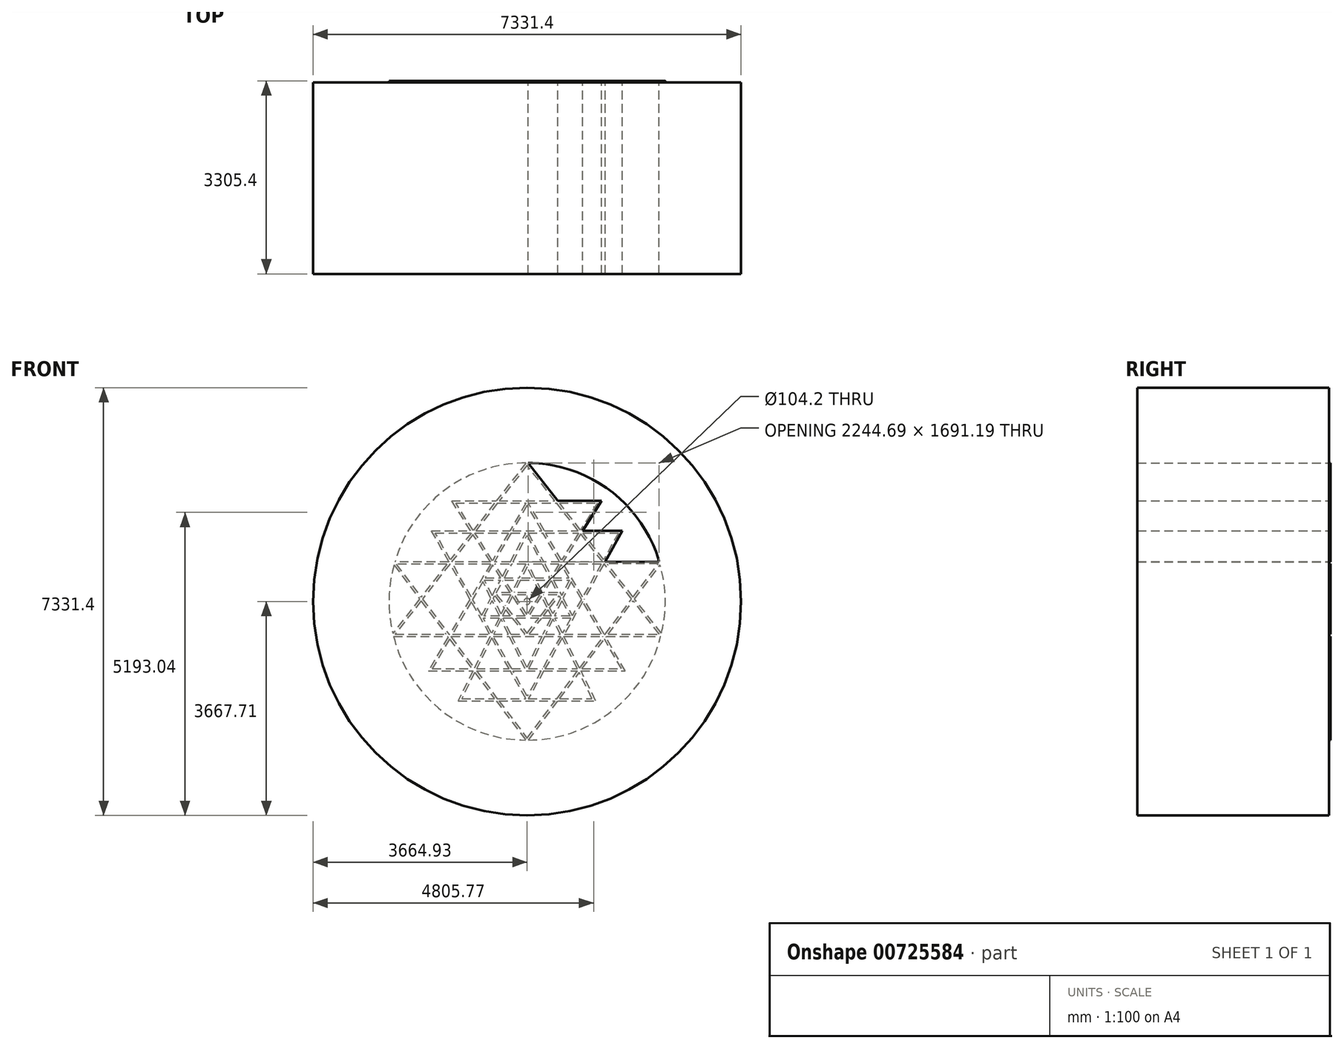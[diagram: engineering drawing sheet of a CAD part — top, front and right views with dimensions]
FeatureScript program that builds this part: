
annotation { "Feature Type Name" : "Feature", "Feature Type Description" : "" }
export const myFeature = defineFeature(function(context is Context, id is Id, definition is map)
    precondition{}
    {
        {
            var Q0;
            Q0=qCreatedBy(makeId("Front.planeOp"),FACE);
            var sketch = newSketch(context, id + "F0", { "sketchPlane" : qUnion([Q0])});
            skCircle(sketch, "E0", {"center": v(-0.77, 2) * mm, "radius": 52.1 * mm});
            skFitSpline(sketch, "E1", {"points": [v(-19.78, 2372.92) * mm, v(-79.06, 2372.42) * mm, v(-211.54, 2366.3) * mm, v(-417.93, 2339.15) * mm, v(-638.47, 2288.55) * mm, v(-858.52, 2214.91) * mm, v(-1074.6, 2117.77) * mm, v(-1283.05, 1997.38) * mm, v(-1480.23, 1854.71) * mm, v(-1662.7, 1691.55) * mm, v(-1827.41, 1510.32) * mm, v(-1971.9, 1314.05) * mm, v(-2094.38, 1106.18) * mm, v(-2192.04, 894.16) * mm, v(-2242.35, 749.81) * mm, v(-2263.3, 679.4) * mm]});
            skLineSegment(sketch, "E2", {"start": v(-1342.2, 680) * mm, "end": v(-2263.3, 679.4) * mm});
            skLineSegment(sketch, "E3", {"start": v(-1339.88, 682.97) * mm, "end": v(-1342.2, 680) * mm});
            skLineSegment(sketch, "E4", {"start": v(-1339.88, 682.97) * mm, "end": v(-1638.44, 1213.98) * mm});
            skLineSegment(sketch, "E5", {"start": v(-1638.44, 1213.98) * mm, "end": v(-965.7, 1213.91) * mm});
            skLineSegment(sketch, "E6", {"start": v(-965.7, 1213.91) * mm, "end": v(-1291.92, 1723.93) * mm});
            skLineSegment(sketch, "E7", {"start": v(-1291.92, 1723.93) * mm, "end": v(-526.88, 1723.75) * mm});
            skLineSegment(sketch, "E8", {"start": v(-19.78, 2372.92) * mm, "end": v(-526.88, 1723.75) * mm});
            skLineSegment(sketch, "E9", {"start": v(2299.72, -542.06) * mm, "end": v(1840.73, 44.25) * mm});
            skFitSpline(sketch, "E10", {"points": [v(2299.72, -542.06) * mm, v(2307.13, -510.36) * mm, v(2329.15, -406.53) * mm, v(2354.3, -230.83) * mm, v(2365.32, -14.98) * mm, v(2357, 201) * mm, v(2329.02, 415.69) * mm, v(2297.2, 557.4) * mm, v(2278.39, 626.42) * mm]});
            skLineSegment(sketch, "E11", {"start": v(1840.73, 44.25) * mm, "end": v(2278.39, 626.42) * mm});
            skLineSegment(sketch, "E12", {"start": v(-2278.19, 627.17) * mm, "end": v(-1839.72, 43.1) * mm});
            skFitSpline(sketch, "E13", {"points": [v(-2278.19, 627.17) * mm, v(-2294.45, 567.53) * mm, v(-2325, 435.53) * mm, v(-2354.3, 230.83) * mm, v(-2365.32, 14.98) * mm, v(-2357, -201) * mm, v(-2332.65, -387.87) * mm, v(-2309, -502.57) * mm, v(-2299.05, -544.93) * mm]});
            skLineSegment(sketch, "E14", {"start": v(-1839.72, 43.1) * mm, "end": v(-2299.05, -544.93) * mm});
            skLineSegment(sketch, "E15", {"start": v(-1816.03, 11.54) * mm, "end": v(-1387.77, -558.94) * mm});
            skLineSegment(sketch, "E16", {"start": v(-1816.03, 11.54) * mm, "end": v(-2261.69, -558.98) * mm});
            skLineSegment(sketch, "E17", {"start": v(-2261.69, -558.98) * mm, "end": v(-1387.77, -558.94) * mm});
            skLineSegment(sketch, "E18", {"start": v(1387.38, -558.81) * mm, "end": v(1817.03, 12.72) * mm});
            skLineSegment(sketch, "E19", {"start": v(1387.38, -558.81) * mm, "end": v(2264.42, -558.77) * mm});
            skLineSegment(sketch, "E20", {"start": v(2264.42, -558.77) * mm, "end": v(1817.03, 12.72) * mm});
            skLineSegment(sketch, "E21", {"start": v(1318.84, -558.82) * mm, "end": v(1339.71, -558.81) * mm});
            skLineSegment(sketch, "E22", {"start": v(1339.71, -558.81) * mm, "end": v(1792.71, 43.78) * mm});
            skLineSegment(sketch, "E23", {"start": v(1792.71, 43.78) * mm, "end": v(1323.12, 643.64) * mm});
            skLineSegment(sketch, "E24", {"start": v(1323.12, 643.64) * mm, "end": v(1313.22, 643.63) * mm});
            skLineSegment(sketch, "E25", {"start": v(1313.22, 643.63) * mm, "end": v(974.08, 38.38) * mm});
            skLineSegment(sketch, "E26", {"start": v(1318.84, -558.82) * mm, "end": v(974.08, 38.38) * mm});
            skLineSegment(sketch, "E27", {"start": v(-976.95, 37.49) * mm, "end": v(-1316.8, 641.91) * mm});
            skLineSegment(sketch, "E28", {"start": v(-1316.8, 641.91) * mm, "end": v(-1323.61, 641.91) * mm});
            skLineSegment(sketch, "E29", {"start": v(-1323.61, 641.91) * mm, "end": v(-1791.73, 42.64) * mm});
            skLineSegment(sketch, "E30", {"start": v(-1791.73, 42.64) * mm, "end": v(-1340.13, -558.94) * mm});
            skLineSegment(sketch, "E31", {"start": v(-1340.13, -558.94) * mm, "end": v(-1322.94, -558.94) * mm});
            skLineSegment(sketch, "E32", {"start": v(-976.95, 37.49) * mm, "end": v(-1322.94, -558.94) * mm});
            skLineSegment(sketch, "E33", {"start": v(-896.66, -1213.15) * mm, "end": v(-559.77, -1661.91) * mm});
            skLineSegment(sketch, "E34", {"start": v(-896.66, -1213.15) * mm, "end": v(-1118.5, -1661.9) * mm});
            skLineSegment(sketch, "E35", {"start": v(-1118.5, -1661.9) * mm, "end": v(-559.77, -1661.91) * mm});
            skLineSegment(sketch, "E36", {"start": v(-483.52, -1700.02) * mm, "end": v(481.78, -1700.05) * mm});
            skLineSegment(sketch, "E37", {"start": v(-483.52, -1700.02) * mm, "end": v(-1.2, -2342.52) * mm});
            skLineSegment(sketch, "E38", {"start": v(-1.2, -2342.52) * mm, "end": v(481.78, -1700.05) * mm});
            skLineSegment(sketch, "E39", {"start": v(1348.61, -610.38) * mm, "end": v(1358.74, -596.91) * mm});
            skLineSegment(sketch, "E40", {"start": v(923.14, -1190.6) * mm, "end": v(1683.58, -1190.6) * mm});
            skLineSegment(sketch, "E41", {"start": v(1683.58, -1190.6) * mm, "end": v(1348.61, -610.38) * mm});
            skLineSegment(sketch, "E42", {"start": v(529.44, -1700.05) * mm, "end": v(1174.16, -1700.08) * mm});
            skLineSegment(sketch, "E43", {"start": v(1174.16, -1700.08) * mm, "end": v(923.14, -1190.6) * mm});
            skLineSegment(sketch, "E44", {"start": v(23.64, -2372.89) * mm, "end": v(529.44, -1700.05) * mm});
            skFitSpline(sketch, "E45", {"points": [v(23.64, -2372.89) * mm, v(81.63, -2372.3) * mm, v(212.81, -2366.13) * mm, v(417.93, -2339.15) * mm, v(638.47, -2288.55) * mm, v(858.52, -2214.91) * mm, v(1074.6, -2117.77) * mm, v(1283.05, -1997.38) * mm, v(1480.23, -1854.71) * mm, v(1662.7, -1691.55) * mm, v(1827.41, -1510.32) * mm, v(1971.9, -1314.05) * mm, v(2094.38, -1106.18) * mm, v(2193.8, -890.35) * mm, v(2253.07, -718.84) * mm, v(2280.13, -620.47) * mm, v(2286.24, -596.87) * mm]});
            skLineSegment(sketch, "E46", {"start": v(1358.74, -596.91) * mm, "end": v(2286.24, -596.87) * mm});
            skLineSegment(sketch, "E47", {"start": v(477.74, 1723.51) * mm, "end": v(-1, 2335.06) * mm});
            skLineSegment(sketch, "E48", {"start": v(-1, 2335.06) * mm, "end": v(-478.54, 1723.74) * mm});
            skLineSegment(sketch, "E49", {"start": v(-478.54, 1723.74) * mm, "end": v(477.74, 1723.51) * mm});
            skLineSegment(sketch, "E50", {"start": v(-556.64, 1685.66) * mm, "end": v(-922.57, 1217.2) * mm});
            skLineSegment(sketch, "E51", {"start": v(-922.57, 1217.2) * mm, "end": v(-1222.3, 1685.81) * mm});
            skLineSegment(sketch, "E52", {"start": v(-1222.3, 1685.81) * mm, "end": v(-556.64, 1685.66) * mm});
            skLineSegment(sketch, "E53", {"start": v(-1359.17, -597.04) * mm, "end": v(-1351.2, -607.65) * mm});
            skLineSegment(sketch, "E54", {"start": v(-2286.18, -597.08) * mm, "end": v(-1359.17, -597.04) * mm});
            skFitSpline(sketch, "E55", {"points": [v(-2286.18, -597.08) * mm, v(-2282.6, -610.96) * mm, v(-2258.74, -699.8) * mm, v(-2204.8, -862.5) * mm, v(-2108.1, -1079.57) * mm, v(-1988.24, -1288.98) * mm, v(-1846.22, -1487.05) * mm, v(-1683.8, -1670.35) * mm, v(-1503.39, -1835.82) * mm, v(-1308.02, -1980.97) * mm, v(-1101.1, -2104) * mm, v(-886.25, -2203.86) * mm, v(-667.14, -2280.28) * mm, v(-447.25, -2333.67) * mm, v(-233.45, -2364.55) * mm, v(-93.17, -2372.12) * mm, v(-26.06, -2372.86) * mm]});
            skLineSegment(sketch, "E56", {"start": v(-531.17, -1700.02) * mm, "end": v(-26.06, -2372.86) * mm});
            skLineSegment(sketch, "E57", {"start": v(-928.02, -1190.61) * mm, "end": v(-1179.84, -1700) * mm});
            skLineSegment(sketch, "E58", {"start": v(-1179.84, -1700) * mm, "end": v(-531.17, -1700.02) * mm});
            skLineSegment(sketch, "E59", {"start": v(-1351.2, -607.65) * mm, "end": v(-1689.38, -1190.62) * mm});
            skLineSegment(sketch, "E60", {"start": v(-1689.38, -1190.62) * mm, "end": v(-928.02, -1190.61) * mm});
            skLineSegment(sketch, "E61", {"start": v(295.52, 1213.78) * mm, "end": v(23.18, 1685.52) * mm});
            skLineSegment(sketch, "E62", {"start": v(295.52, 1213.78) * mm, "end": v(876.83, 1213.72) * mm});
            skLineSegment(sketch, "E63", {"start": v(876.83, 1213.72) * mm, "end": v(507.57, 1685.4) * mm});
            skLineSegment(sketch, "E64", {"start": v(23.18, 1685.52) * mm, "end": v(507.57, 1685.4) * mm});
            skLineSegment(sketch, "E65", {"start": v(526.14, 1723.5) * mm, "end": v(1275.7, 1723.33) * mm});
            skLineSegment(sketch, "E66", {"start": v(1275.7, 1723.33) * mm, "end": v(952.94, 1213.7) * mm});
            skLineSegment(sketch, "E67", {"start": v(952.94, 1213.7) * mm, "end": v(1632.62, 1213.64) * mm});
            skLineSegment(sketch, "E68", {"start": v(1632.62, 1213.64) * mm, "end": v(1337.54, 687.02) * mm});
            skLineSegment(sketch, "E69", {"start": v(1341.67, 681.75) * mm, "end": v(1337.54, 687.02) * mm});
            skLineSegment(sketch, "E70", {"start": v(2262.42, 682.35) * mm, "end": v(1341.67, 681.75) * mm});
            skFitSpline(sketch, "E71", {"points": [v(2262.42, 682.35) * mm, v(2244.53, 742.2) * mm, v(2198.6, 876.38) * mm, v(2108.1, 1079.57) * mm, v(1988.24, 1288.98) * mm, v(1846.22, 1487.05) * mm, v(1683.8, 1670.35) * mm, v(1503.39, 1835.82) * mm, v(1308.02, 1980.97) * mm, v(1101.1, 2104) * mm, v(886.25, 2203.86) * mm, v(667.14, 2280.28) * mm, v(447.25, 2333.67) * mm, v(230.7, 2364.95) * mm, v(87.62, 2372.41) * mm, v(17.73, 2372.94) * mm]});
            skLineSegment(sketch, "E72", {"start": v(526.14, 1723.5) * mm, "end": v(17.73, 2372.94) * mm});
            skLineSegment(sketch, "E73", {"start": v(1290.9, 681.71) * mm, "end": v(615.72, 681.27) * mm});
            skLineSegment(sketch, "E74", {"start": v(1291.9, 683.51) * mm, "end": v(1290.9, 681.71) * mm});
            skLineSegment(sketch, "E75", {"start": v(1291.9, 683.51) * mm, "end": v(918.9, 1159.97) * mm});
            skLineSegment(sketch, "E76", {"start": v(918.9, 1159.97) * mm, "end": v(615.72, 681.27) * mm});
            skLineSegment(sketch, "E77", {"start": v(1816.42, 75.3) * mm, "end": v(2244.11, 644.24) * mm});
            skLineSegment(sketch, "E78", {"start": v(2244.11, 644.24) * mm, "end": v(1371.48, 643.67) * mm});
            skLineSegment(sketch, "E79", {"start": v(1816.42, 75.3) * mm, "end": v(1371.48, 643.67) * mm});
            skLineSegment(sketch, "E80", {"start": v(955.05, 1175.6) * mm, "end": v(1567.6, 1175.54) * mm});
            skLineSegment(sketch, "E81", {"start": v(1567.6, 1175.54) * mm, "end": v(1312.08, 719.54) * mm});
            skLineSegment(sketch, "E82", {"start": v(1312.08, 719.54) * mm, "end": v(955.05, 1175.6) * mm});
            skLineSegment(sketch, "E83", {"start": v(21.32, -1661.94) * mm, "end": v(510.42, -1661.95) * mm});
            skLineSegment(sketch, "E84", {"start": v(285.43, -1190.6) * mm, "end": v(21.32, -1661.94) * mm});
            skLineSegment(sketch, "E85", {"start": v(285.43, -1190.6) * mm, "end": v(864.76, -1190.6) * mm});
            skLineSegment(sketch, "E86", {"start": v(510.42, -1661.95) * mm, "end": v(864.76, -1190.6) * mm});
            skLineSegment(sketch, "E87", {"start": v(-896.1, 1175.8) * mm, "end": v(-316.65, 1175.74) * mm});
            skLineSegment(sketch, "E88", {"start": v(-592.22, 700.7) * mm, "end": v(-896.1, 1175.8) * mm});
            skLineSegment(sketch, "E89", {"start": v(-316.65, 1175.74) * mm, "end": v(-592.22, 700.7) * mm});
            skLineSegment(sketch, "E90", {"start": v(-250.5, 1213.84) * mm, "end": v(251.52, 1213.78) * mm});
            skLineSegment(sketch, "E91", {"start": v(251.52, 1213.78) * mm, "end": v(1.1, 1647.56) * mm});
            skLineSegment(sketch, "E92", {"start": v(1.1, 1647.56) * mm, "end": v(-250.5, 1213.84) * mm});
            skLineSegment(sketch, "E93", {"start": v(587.53, 707.96) * mm, "end": v(317.51, 1175.68) * mm});
            skLineSegment(sketch, "E94", {"start": v(883.72, 1175.62) * mm, "end": v(587.53, 707.96) * mm});
            skLineSegment(sketch, "E95", {"start": v(317.51, 1175.68) * mm, "end": v(883.72, 1175.62) * mm});
            skLineSegment(sketch, "E96", {"start": v(-1314.47, 715.51) * mm, "end": v(-1573.3, 1175.88) * mm});
            skLineSegment(sketch, "E97", {"start": v(-1573.3, 1175.88) * mm, "end": v(-954.9, 1175.81) * mm});
            skLineSegment(sketch, "E98", {"start": v(-954.9, 1175.81) * mm, "end": v(-1314.47, 715.51) * mm});
            skLineSegment(sketch, "E99", {"start": v(-272.6, 1175.74) * mm, "end": v(-559.89, 680.5) * mm});
            skLineSegment(sketch, "E100", {"start": v(-272.6, 1175.74) * mm, "end": v(-21.74, 1175.71) * mm});
            skLineSegment(sketch, "E101", {"start": v(-286.71, 680.69) * mm, "end": v(-21.74, 1175.71) * mm});
            skLineSegment(sketch, "E102", {"start": v(-286.71, 680.69) * mm, "end": v(-559.89, 680.5) * mm});
            skLineSegment(sketch, "E103", {"start": v(1269.53, 643.6) * mm, "end": v(624.93, 643.18) * mm});
            skLineSegment(sketch, "E104", {"start": v(1269.53, 643.6) * mm, "end": v(951.92, 76.77) * mm});
            skLineSegment(sketch, "E105", {"start": v(951.92, 76.77) * mm, "end": v(624.93, 643.18) * mm});
            skLineSegment(sketch, "E106", {"start": v(555.97, 1685.4) * mm, "end": v(1206.49, 1685.24) * mm});
            skLineSegment(sketch, "E107", {"start": v(1206.49, 1685.24) * mm, "end": v(915.62, 1225.98) * mm});
            skLineSegment(sketch, "E108", {"start": v(915.62, 1225.98) * mm, "end": v(555.97, 1685.4) * mm});
            skLineSegment(sketch, "E109", {"start": v(-626.06, 642.37) * mm, "end": v(-954.76, 75.75) * mm});
            skLineSegment(sketch, "E110", {"start": v(-626.06, 642.37) * mm, "end": v(-1273.1, 641.94) * mm});
            skLineSegment(sketch, "E111", {"start": v(-954.76, 75.75) * mm, "end": v(-1273.1, 641.94) * mm});
            skLineSegment(sketch, "E112", {"start": v(1274.85, -558.82) * mm, "end": v(952.41, -0.29) * mm});
            skLineSegment(sketch, "E113", {"start": v(639.43, -558.85) * mm, "end": v(1274.85, -558.82) * mm});
            skLineSegment(sketch, "E114", {"start": v(952.41, -0.29) * mm, "end": v(639.43, -558.85) * mm});
            skLineSegment(sketch, "E115", {"start": v(-955.27, -1.07) * mm, "end": v(-1278.9, -558.94) * mm});
            skLineSegment(sketch, "E116", {"start": v(-641.63, -558.9) * mm, "end": v(-955.27, -1.07) * mm});
            skLineSegment(sketch, "E117", {"start": v(-1278.9, -558.94) * mm, "end": v(-641.63, -558.9) * mm});
            skLineSegment(sketch, "E118", {"start": v(-508.3, 1685.65) * mm, "end": v(-876.8, 1213.9) * mm});
            skLineSegment(sketch, "E119", {"start": v(-876.8, 1213.9) * mm, "end": v(-294.55, 1213.84) * mm});
            skLineSegment(sketch, "E120", {"start": v(-20.92, 1685.53) * mm, "end": v(-294.55, 1213.84) * mm});
            skLineSegment(sketch, "E121", {"start": v(-508.3, 1685.65) * mm, "end": v(-20.92, 1685.53) * mm});
            skLineSegment(sketch, "E122", {"start": v(-925.68, 1151.34) * mm, "end": v(-1293.84, 680.03) * mm});
            skLineSegment(sketch, "E123", {"start": v(-624.5, 680.47) * mm, "end": v(-925.68, 1151.34) * mm});
            skLineSegment(sketch, "E124", {"start": v(-624.5, 680.47) * mm, "end": v(-1293.84, 680.03) * mm});
            skLineSegment(sketch, "E125", {"start": v(900.02, -1143.7) * mm, "end": v(630.64, -596.95) * mm});
            skLineSegment(sketch, "E126", {"start": v(630.64, -596.95) * mm, "end": v(1296.85, -596.92) * mm});
            skLineSegment(sketch, "E127", {"start": v(1303.02, -607.62) * mm, "end": v(1296.85, -596.92) * mm});
            skLineSegment(sketch, "E128", {"start": v(900.02, -1143.7) * mm, "end": v(1303.02, -607.62) * mm});
            skLineSegment(sketch, "E129", {"start": v(941.07, -1152.5) * mm, "end": v(1617.59, -1152.5) * mm});
            skLineSegment(sketch, "E130", {"start": v(1617.59, -1152.5) * mm, "end": v(1323.73, -643.48) * mm});
            skLineSegment(sketch, "E131", {"start": v(941.07, -1152.5) * mm, "end": v(1323.73, -643.48) * mm});
            skLineSegment(sketch, "E132", {"start": v(-1305.59, -604.95) * mm, "end": v(-903.37, -1140.75) * mm});
            skLineSegment(sketch, "E133", {"start": v(-1301, -597.04) * mm, "end": v(-1305.59, -604.95) * mm});
            skLineSegment(sketch, "E134", {"start": v(-1301, -597.04) * mm, "end": v(-634.56, -597) * mm});
            skLineSegment(sketch, "E135", {"start": v(-634.56, -597) * mm, "end": v(-903.37, -1140.75) * mm});
            skLineSegment(sketch, "E136", {"start": v(602.16, -625.36) * mm, "end": v(306.77, -1152.5) * mm});
            skLineSegment(sketch, "E137", {"start": v(861.9, -1152.5) * mm, "end": v(602.16, -625.36) * mm});
            skLineSegment(sketch, "E138", {"start": v(306.77, -1152.5) * mm, "end": v(861.9, -1152.5) * mm});
            skLineSegment(sketch, "E139", {"start": v(558.08, -1661.95) * mm, "end": v(893.24, -1216.13) * mm});
            skLineSegment(sketch, "E140", {"start": v(558.08, -1661.95) * mm, "end": v(1112.91, -1661.97) * mm});
            skLineSegment(sketch, "E141", {"start": v(1112.91, -1661.97) * mm, "end": v(893.24, -1216.13) * mm});
            skLineSegment(sketch, "E142", {"start": v(-242.74, -1190.61) * mm, "end": v(241.75, -1190.6) * mm});
            skLineSegment(sketch, "E143", {"start": v(241.75, -1190.6) * mm, "end": v(-0.08, -1622.2) * mm});
            skLineSegment(sketch, "E144", {"start": v(-0.08, -1622.2) * mm, "end": v(-242.74, -1190.61) * mm});
            skLineSegment(sketch, "E145", {"start": v(-866.68, -1152.51) * mm, "end": v(-307.87, -1152.51) * mm});
            skLineSegment(sketch, "E146", {"start": v(-605.23, -623.65) * mm, "end": v(-866.68, -1152.51) * mm});
            skLineSegment(sketch, "E147", {"start": v(-307.87, -1152.51) * mm, "end": v(-605.23, -623.65) * mm});
            skLineSegment(sketch, "E148", {"start": v(-865.93, -1190.61) * mm, "end": v(-512.13, -1661.92) * mm});
            skLineSegment(sketch, "E149", {"start": v(-512.13, -1661.92) * mm, "end": v(-21.45, -1661.93) * mm});
            skLineSegment(sketch, "E150", {"start": v(-21.45, -1661.93) * mm, "end": v(-286.45, -1190.61) * mm});
            skLineSegment(sketch, "E151", {"start": v(-865.93, -1190.61) * mm, "end": v(-286.45, -1190.61) * mm});
            skLineSegment(sketch, "E152", {"start": v(-1326.36, -640.75) * mm, "end": v(-942.17, -1152.51) * mm});
            skLineSegment(sketch, "E153", {"start": v(-1326.36, -640.75) * mm, "end": v(-1623.23, -1152.52) * mm});
            skLineSegment(sketch, "E154", {"start": v(-1623.23, -1152.52) * mm, "end": v(-942.17, -1152.51) * mm});
            skLineSegment(sketch, "E155", {"start": v(-1371.98, 641.88) * mm, "end": v(-2241.16, 641.31) * mm});
            skLineSegment(sketch, "E156", {"start": v(-2241.16, 641.31) * mm, "end": v(-1815.43, 74.2) * mm});
            skLineSegment(sketch, "E157", {"start": v(-1371.98, 641.88) * mm, "end": v(-1815.43, 74.2) * mm});
            skLineSegment(sketch, "E158", {"start": v(-479.62, -283.6) * mm, "end": v(-607.4, -542.06) * mm});
            skLineSegment(sketch, "E159", {"start": v(-607.4, -542.06) * mm, "end": v(-752.7, -283.62) * mm});
            skLineSegment(sketch, "E160", {"start": v(-479.62, -283.6) * mm, "end": v(-752.7, -283.62) * mm});
            skLineSegment(sketch, "E161", {"start": v(-778.4, -237.9) * mm, "end": v(-933.08, 37.2) * mm});
            skLineSegment(sketch, "E162", {"start": v(-778.4, -237.9) * mm, "end": v(-619.93, 58.16) * mm});
            skLineSegment(sketch, "E163", {"start": v(-619.93, 58.16) * mm, "end": v(-756.76, 341.13) * mm});
            skLineSegment(sketch, "E164", {"start": v(-756.76, 341.13) * mm, "end": v(-933.08, 37.2) * mm});
            skLineSegment(sketch, "E165", {"start": v(930.25, 38.1) * mm, "end": v(754.3, 342.9) * mm});
            skLineSegment(sketch, "E166", {"start": v(930.25, 38.1) * mm, "end": v(774.05, -240.65) * mm});
            skLineSegment(sketch, "E167", {"start": v(615.34, 57.05) * mm, "end": v(774.05, -240.65) * mm});
            skLineSegment(sketch, "E168", {"start": v(754.3, 342.9) * mm, "end": v(615.34, 57.05) * mm});
            skLineSegment(sketch, "E169", {"start": v(-420.06, 431.56) * mm, "end": v(-554.93, 642.41) * mm});
            skLineSegment(sketch, "E170", {"start": v(-420.06, 431.56) * mm, "end": v(-307.11, 642.57) * mm});
            skLineSegment(sketch, "E171", {"start": v(-307.11, 642.57) * mm, "end": v(-554.93, 642.41) * mm});
            skLineSegment(sketch, "E172", {"start": v(558.96, 681.24) * mm, "end": v(282.67, 681.06) * mm});
            skLineSegment(sketch, "E173", {"start": v(18.97, 1175.7) * mm, "end": v(282.67, 681.06) * mm});
            skLineSegment(sketch, "E174", {"start": v(18.97, 1175.7) * mm, "end": v(273.52, 1175.68) * mm});
            skLineSegment(sketch, "E175", {"start": v(558.96, 681.24) * mm, "end": v(273.52, 1175.68) * mm});
            skLineSegment(sketch, "E176", {"start": v(239.51, 681.03) * mm, "end": v(-243.48, 680.71) * mm});
            skLineSegment(sketch, "E177", {"start": v(-243.48, 680.71) * mm, "end": v(-1.41, 1132.95) * mm});
            skLineSegment(sketch, "E178", {"start": v(-1.41, 1132.95) * mm, "end": v(239.51, 681.03) * mm});
            skLineSegment(sketch, "E179", {"start": v(-389.48, 407.96) * mm, "end": v(-137.78, 407.86) * mm});
            skLineSegment(sketch, "E180", {"start": v(-389.48, 407.96) * mm, "end": v(-263.88, 642.6) * mm});
            skLineSegment(sketch, "E181", {"start": v(-21.65, 642.76) * mm, "end": v(-263.88, 642.6) * mm});
            skLineSegment(sketch, "E182", {"start": v(-21.65, 642.76) * mm, "end": v(-137.78, 407.86) * mm});
            skLineSegment(sketch, "E183", {"start": v(574.4, -596.95) * mm, "end": v(263.1, -1152.5) * mm});
            skLineSegment(sketch, "E184", {"start": v(297.42, -596.96) * mm, "end": v(574.4, -596.95) * mm});
            skLineSegment(sketch, "E185", {"start": v(297.42, -596.96) * mm, "end": v(27.36, -1152.51) * mm});
            skLineSegment(sketch, "E186", {"start": v(27.36, -1152.51) * mm, "end": v(263.1, -1152.5) * mm});
            skLineSegment(sketch, "E187", {"start": v(-264.16, -1152.51) * mm, "end": v(-576.5, -597) * mm});
            skLineSegment(sketch, "E188", {"start": v(-576.5, -597) * mm, "end": v(-303.14, -597) * mm});
            skLineSegment(sketch, "E189", {"start": v(-34.52, -1152.51) * mm, "end": v(-303.14, -597) * mm});
            skLineSegment(sketch, "E190", {"start": v(-264.16, -1152.51) * mm, "end": v(-34.52, -1152.51) * mm});
            skLineSegment(sketch, "E191", {"start": v(255.05, -596.97) * mm, "end": v(-3.57, -1128.99) * mm});
            skLineSegment(sketch, "E192", {"start": v(-3.57, -1128.99) * mm, "end": v(-260.82, -596.99) * mm});
            skLineSegment(sketch, "E193", {"start": v(-260.82, -596.99) * mm, "end": v(255.05, -596.97) * mm});
            skLineSegment(sketch, "E194", {"start": v(315.94, -558.86) * mm, "end": v(569.4, -558.85) * mm});
            skLineSegment(sketch, "E195", {"start": v(441.81, -299.92) * mm, "end": v(315.94, -558.86) * mm});
            skLineSegment(sketch, "E196", {"start": v(569.4, -558.85) * mm, "end": v(441.81, -299.92) * mm});
            skLineSegment(sketch, "E197", {"start": v(546.46, 643.13) * mm, "end": v(302.98, 642.97) * mm});
            skLineSegment(sketch, "E198", {"start": v(546.46, 643.13) * mm, "end": v(414.21, 434.32) * mm});
            skLineSegment(sketch, "E199", {"start": v(302.98, 642.97) * mm, "end": v(414.21, 434.32) * mm});
            skLineSegment(sketch, "E200", {"start": v(-573.22, -558.9) * mm, "end": v(-321.56, -558.9) * mm});
            skLineSegment(sketch, "E201", {"start": v(-446, -301.56) * mm, "end": v(-573.22, -558.9) * mm});
            skLineSegment(sketch, "E202", {"start": v(-321.56, -558.9) * mm, "end": v(-446, -301.56) * mm});
            skLineSegment(sketch, "E203", {"start": v(-473.1, -245.5) * mm, "end": v(-739.27, -245.52) * mm});
            skLineSegment(sketch, "E204", {"start": v(-739.27, -245.52) * mm, "end": v(-599.42, 15.75) * mm});
            skLineSegment(sketch, "E205", {"start": v(-473.1, -245.5) * mm, "end": v(-599.42, 15.75) * mm});
            skLineSegment(sketch, "E206", {"start": v(-590.63, 627.52) * mm, "end": v(-717.91, 408.1) * mm});
            skLineSegment(sketch, "E207", {"start": v(-450.22, 407.99) * mm, "end": v(-590.63, 627.52) * mm});
            skLineSegment(sketch, "E208", {"start": v(-717.91, 408.1) * mm, "end": v(-450.22, 407.99) * mm});
            skLineSegment(sketch, "E209", {"start": v(-597.7, 99.7) * mm, "end": v(-453.07, 369.9) * mm});
            skLineSegment(sketch, "E210", {"start": v(-597.7, 99.7) * mm, "end": v(-728.4, 370) * mm});
            skLineSegment(sketch, "E211", {"start": v(-728.4, 370) * mm, "end": v(-453.07, 369.9) * mm});
            skLineSegment(sketch, "E212", {"start": v(-156.61, 369.77) * mm, "end": v(-254.23, 172.3) * mm});
            skLineSegment(sketch, "E213", {"start": v(-380.6, 369.86) * mm, "end": v(-156.61, 369.77) * mm});
            skLineSegment(sketch, "E214", {"start": v(-254.23, 172.3) * mm, "end": v(-380.6, 369.86) * mm});
            skLineSegment(sketch, "E215", {"start": v(-279.24, -558.9) * mm, "end": v(-412.36, -283.6) * mm});
            skLineSegment(sketch, "E216", {"start": v(-254.82, -283.59) * mm, "end": v(-412.36, -283.6) * mm});
            skLineSegment(sketch, "E217", {"start": v(-254.82, -283.59) * mm, "end": v(-39.52, -558.88) * mm});
            skLineSegment(sketch, "E218", {"start": v(-279.24, -558.9) * mm, "end": v(-39.52, -558.88) * mm});
            skLineSegment(sketch, "E219", {"start": v(-95.29, 407.84) * mm, "end": v(93.13, 407.76) * mm});
            skLineSegment(sketch, "E220", {"start": v(93.13, 407.76) * mm, "end": v(-0.94, 598.68) * mm});
            skLineSegment(sketch, "E221", {"start": v(-0.94, 598.68) * mm, "end": v(-95.29, 407.84) * mm});
            skLineSegment(sketch, "E222", {"start": v(259.82, 642.94) * mm, "end": v(385.26, 407.64) * mm});
            skLineSegment(sketch, "E223", {"start": v(135.61, 407.74) * mm, "end": v(385.26, 407.64) * mm});
            skLineSegment(sketch, "E224", {"start": v(135.61, 407.74) * mm, "end": v(19.8, 642.79) * mm});
            skLineSegment(sketch, "E225", {"start": v(259.82, 642.94) * mm, "end": v(19.8, 642.79) * mm});
            skLineSegment(sketch, "E226", {"start": v(594.75, 14.69) * mm, "end": v(733.42, -245.42) * mm});
            skLineSegment(sketch, "E227", {"start": v(733.42, -245.42) * mm, "end": v(468.3, -245.44) * mm});
            skLineSegment(sketch, "E228", {"start": v(594.75, 14.69) * mm, "end": v(468.3, -245.44) * mm});
            skLineSegment(sketch, "E229", {"start": v(604.33, -543.55) * mm, "end": v(476.22, -283.54) * mm});
            skLineSegment(sketch, "E230", {"start": v(750.03, -283.52) * mm, "end": v(604.33, -543.55) * mm});
            skLineSegment(sketch, "E231", {"start": v(750.03, -283.52) * mm, "end": v(476.22, -283.54) * mm});
            skLineSegment(sketch, "E232", {"start": v(37.65, -558.88) * mm, "end": v(251.49, -283.55) * mm});
            skLineSegment(sketch, "E233", {"start": v(407.41, -283.54) * mm, "end": v(251.49, -283.55) * mm});
            skLineSegment(sketch, "E234", {"start": v(407.41, -283.54) * mm, "end": v(273.57, -558.86) * mm});
            skLineSegment(sketch, "E235", {"start": v(37.65, -558.88) * mm, "end": v(273.57, -558.86) * mm});
            skLineSegment(sketch, "E236", {"start": v(448.76, 369.51) * mm, "end": v(724.81, 369.4) * mm});
            skLineSegment(sketch, "E237", {"start": v(724.81, 369.4) * mm, "end": v(593.18, 98.61) * mm});
            skLineSegment(sketch, "E238", {"start": v(448.76, 369.51) * mm, "end": v(593.18, 98.61) * mm});
            skLineSegment(sketch, "E239", {"start": v(373.19, 369.54) * mm, "end": v(250.15, 175.28) * mm});
            skLineSegment(sketch, "E240", {"start": v(154.39, 369.64) * mm, "end": v(373.19, 369.54) * mm});
            skLineSegment(sketch, "E241", {"start": v(250.15, 175.28) * mm, "end": v(154.39, 369.64) * mm});
            skLineSegment(sketch, "E242", {"start": v(-554.53, 99.62) * mm, "end": v(-392.55, -107.49) * mm});
            skLineSegment(sketch, "E243", {"start": v(-577.19, 57.28) * mm, "end": v(-554.53, 99.62) * mm});
            skLineSegment(sketch, "E244", {"start": v(-445.61, -214.82) * mm, "end": v(-577.19, 57.28) * mm});
            skLineSegment(sketch, "E245", {"start": v(-392.55, -107.49) * mm, "end": v(-445.61, -214.82) * mm});
            skLineSegment(sketch, "E246", {"start": v(-288.1, 154.53) * mm, "end": v(-525.1, 154.59) * mm});
            skLineSegment(sketch, "E247", {"start": v(-525.1, 154.59) * mm, "end": v(-417.14, 356.28) * mm});
            skLineSegment(sketch, "E248", {"start": v(-288.1, 154.53) * mm, "end": v(-417.14, 356.28) * mm});
            skLineSegment(sketch, "E249", {"start": v(232.84, -245.46) * mm, "end": v(344.28, -101.97) * mm});
            skLineSegment(sketch, "E250", {"start": v(344.28, -101.97) * mm, "end": v(246, 97.5) * mm});
            skLineSegment(sketch, "E251", {"start": v(246, 97.5) * mm, "end": v(28.77, -245.47) * mm});
            skLineSegment(sketch, "E252", {"start": v(232.84, -245.46) * mm, "end": v(28.77, -245.47) * mm});
            skLineSegment(sketch, "E253", {"start": v(-249.98, 94.93) * mm, "end": v(-347.78, -102.9) * mm});
            skLineSegment(sketch, "E254", {"start": v(-32.25, -245.47) * mm, "end": v(-249.98, 94.93) * mm});
            skLineSegment(sketch, "E255", {"start": v(-32.25, -245.47) * mm, "end": v(-236.26, -245.49) * mm});
            skLineSegment(sketch, "E256", {"start": v(-347.78, -102.9) * mm, "end": v(-236.26, -245.49) * mm});
            skLineSegment(sketch, "E257", {"start": v(-366.51, -140.79) * mm, "end": v(-418.28, -245.5) * mm});
            skLineSegment(sketch, "E258", {"start": v(-366.51, -140.79) * mm, "end": v(-284.62, -245.49) * mm});
            skLineSegment(sketch, "E259", {"start": v(-284.62, -245.49) * mm, "end": v(-418.28, -245.5) * mm});
            skLineSegment(sketch, "E260", {"start": v(442.4, 407.62) * mm, "end": v(717, 407.5) * mm});
            skLineSegment(sketch, "E261", {"start": v(586.02, 634.37) * mm, "end": v(442.4, 407.62) * mm});
            skLineSegment(sketch, "E262", {"start": v(717, 407.5) * mm, "end": v(586.02, 634.37) * mm});
            skLineSegment(sketch, "E263", {"start": v(-114.12, 369.75) * mm, "end": v(111.9, 369.65) * mm});
            skLineSegment(sketch, "E264", {"start": v(217.97, 154.4) * mm, "end": v(111.9, 369.65) * mm});
            skLineSegment(sketch, "E265", {"start": v(217.97, 154.4) * mm, "end": v(-220.53, 154.51) * mm});
            skLineSegment(sketch, "E266", {"start": v(-114.12, 369.75) * mm, "end": v(-220.53, 154.51) * mm});
            skLineSegment(sketch, "E267", {"start": v(414.97, -245.44) * mm, "end": v(281.08, -245.45) * mm});
            skLineSegment(sketch, "E268", {"start": v(281.08, -245.45) * mm, "end": v(363, -139.98) * mm});
            skLineSegment(sketch, "E269", {"start": v(414.97, -245.44) * mm, "end": v(363, -139.98) * mm});
            skLineSegment(sketch, "E270", {"start": v(-206.46, -283.58) * mm, "end": v(-0.9, -546.4) * mm});
            skLineSegment(sketch, "E271", {"start": v(-0.9, -546.4) * mm, "end": v(203.25, -283.56) * mm});
            skLineSegment(sketch, "E272", {"start": v(203.25, -283.56) * mm, "end": v(-206.46, -283.58) * mm});
            skLineSegment(sketch, "E273", {"start": v(-281.85, 116.43) * mm, "end": v(-373.82, -69.6) * mm});
            skLineSegment(sketch, "E274", {"start": v(-281.85, 116.43) * mm, "end": v(-519.36, 116.49) * mm});
            skLineSegment(sketch, "E275", {"start": v(-519.36, 116.49) * mm, "end": v(-373.82, -69.6) * mm});
            skLineSegment(sketch, "E276", {"start": v(549.32, 99.9) * mm, "end": v(572.59, 56.25) * mm});
            skLineSegment(sketch, "E277", {"start": v(389, -106.52) * mm, "end": v(549.32, 99.9) * mm});
            skLineSegment(sketch, "E278", {"start": v(441.58, -213.25) * mm, "end": v(389, -106.52) * mm});
            skLineSegment(sketch, "E279", {"start": v(572.59, 56.25) * mm, "end": v(441.58, -213.25) * mm});
            skLineSegment(sketch, "E280", {"start": v(212.8, 116.3) * mm, "end": v(-1.75, -222.45) * mm});
            skLineSegment(sketch, "E281", {"start": v(-1.75, -222.45) * mm, "end": v(-218.49, 116.4) * mm});
            skLineSegment(sketch, "E282", {"start": v(212.8, 116.3) * mm, "end": v(-218.49, 116.4) * mm});
            skLineSegment(sketch, "E283", {"start": v(370.27, -68.51) * mm, "end": v(279.22, 116.28) * mm});
            skLineSegment(sketch, "E284", {"start": v(370.27, -68.51) * mm, "end": v(513.75, 116.22) * mm});
            skLineSegment(sketch, "E285", {"start": v(513.75, 116.22) * mm, "end": v(279.22, 116.28) * mm});
            skLineSegment(sketch, "E286", {"start": v(411.38, 358.64) * mm, "end": v(520.3, 154.32) * mm});
            skLineSegment(sketch, "E287", {"start": v(411.38, 358.64) * mm, "end": v(282.01, 154.38) * mm});
            skLineSegment(sketch, "E288", {"start": v(520.3, 154.32) * mm, "end": v(282.01, 154.38) * mm});
            skSolve(sketch);
        }
        {
            var Q0;
            Q0 = qSketchRegion(id + "F0", true);
            extrude(context, id + "F1", {"entities" : qUnion([Q0]), "depth" : 25.4 * mm, "offsetDistance" : 25.4 * mm});
        }
        {
            var Q0;
            Q0=makeQuery(id+"F1.opExtrude","CAP_FACE",FACE,{"disambiguationData":[OSD([sQuery(id+"F0.wireOp",EDGE,"E65"),sQuery(id+"F0.wireOp",EDGE,"E66"),sQuery(id+"F0.wireOp",EDGE,"E67"),sQuery(id+"F0.wireOp",EDGE,"E68"),sQuery(id+"F0.wireOp",EDGE,"E69"),sQuery(id+"F0.wireOp",EDGE,"E70"),sQuery(id+"F0.wireOp",EDGE,"E71"),sQuery(id+"F0.wireOp",EDGE,"E72")])],"isStart":false});
            var sketch = newSketch(context, id + "F2", { "sketchPlane" : qUnion([Q0])});
            skCircle(sketch, "E289", {"center": v(0, 0) * mm, "radius": 3665.7 * mm});
            skSolve(sketch);
        }
        {
            var Q0;
            Q0=makeQuery(id+"F2.imprint","IMPRINT",FACE,{"disambiguationData":[TD([[makeQuery(id+"F2.imprint","IMPRINT",EDGE,{"derivedFrom":sQuery(id+"F2.wireOp",EDGE,"E289")}),1.0]])]});
            extrude(context, id + "F3", {"entities" : qUnion([Q0]), "depth" : 3280 * mm, "offsetDistance" : 25 * mm});
        }
    });
